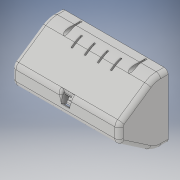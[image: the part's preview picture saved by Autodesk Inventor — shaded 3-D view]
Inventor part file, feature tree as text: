
AUTODESK INVENTOR PART (.ipt)
format: ipt  version: 2018 (Build 220112000, 112)  size: 763,904 bytes
history: native  units: in
note: dims shown in document units (in); Inventor stores cm internally (conversion verified against a paired STEP export)
features: extrude x20, sketch x19, fillet x11, chamfer x5, plane x3, draft x2, shell x1
ambient origin geometry x8: Origin, YZ Plane, XZ Plane, XY Plane, X Axis, Y Axis, Z Axis, Center Point
bodies: Solid1 (feature_tree)
feature tree (61):
  extrude  "Extrusion1"  Depth=3.5in
  shell  "Shell1"  Thickness=0.5in
  extrude  "Extrusion2"  Depth=7.6772in TaperAngle=0.0deg
  fillet  "Fillet4"  Radius=0.25in
  fillet  "Fillet5"  Radius=0.25in
  fillet  "Fillet6"  Radius=0.25in
  plane  "Work Plane1"
  extrude  "Extrusion3"  Depth=7.6772in TaperAngle=0.0deg
  extrude  "Extrusion4"  Depth=1.0in
  extrude  "Extrusion5"  Depth=0.315in
  extrude  "Extrusion6"  TaperAngle=90.0deg  [1 undecoded]
  plane  "Work Plane2"
  fillet  "Fillet13"  Radius=0.5157in
  fillet  "Fillet14"  Radius=0.6496in
  extrude  "Extrusion8"  Depth=1.0in TaperAngle=0.0deg
  extrude  "Extrusion9"  Depth=0.6496in
  extrude  "Extrusion10"  Depth=0.5in
  extrude  "Extrusion11"  Depth=0.5in
  extrude  "Extrusion12"  Depth=0.5709in TaperAngle=0.0deg
  chamfer  "Chamfer4"  Distance=0.2756in
  extrude  "Extrusion13"  Depth=0.1969in
  plane  "Work Plane3"
  extrude  "Extrusion15"  Depth=6.5in
  extrude  "Extrusion16"  Depth=0.125in TaperAngle=0.0deg
  fillet  "Fillet15"  Radius=0.25in
  chamfer  "Chamfer5"  Distance=0.125in
  extrude  "Extrusion17"  Depth=0.1181in
  fillet  "Fillet16"  Radius=0.1181in
  extrude  "Extrusion22"  Depth=0.5in TaperAngle=0.0deg
  extrude  "Extrusion23"  Depth=0.1181in
  fillet  "Fillet22"  Radius=0.7874in
  fillet  "Fillet23"  Radius=0.5in
  chamfer  "Chamfer7"  Distance=0.7874in
  fillet  "Fillet24"  Radius=1.0in
  fillet  "Fillet25"  Radius=0.1181in
  chamfer  "Chamfer9"  Distance=0.7874in
  chamfer  "Chamfer10"  Distance=1.0in
  extrude  "Extrusion27"  Depth=0.1181in
  extrude  "Extrusion28"  Depth=0.7874in
  draft  "FaceDraft1"
  draft  "FaceDraft2"
  extrude  "Extrusion14"  Depth=0.0394in
  sketch  "Sketch1"  dims[d0=4.4094in d1=3.5in d2=0.5in]
  sketch  "Sketch2"  dims[d3=0.5in d4=7.6772in d5=0.0in d6=0.25in d7=0.25in d8=0.25in]
  sketch  "Sketch4"  dims[d10=0.25in d11=7.6772in d12=0.0in]
  sketch  "Sketch5"  dims[d13=1.0in d14=1.0in]
  sketch  "Sketch6"  dims[d18=0.4724in d19=0.315in]
  sketch  "Sketch8"  dims[d20=1.5748in d21=90.0deg d22=0.5157in d23=0.6496in]
  sketch  "Sketch9"  dims[d24=0.1969in d25=1.0in d26=0.0in]
  sketch  "Sketch10"  dims[d27=0.5157in d28=0.6496in]
  sketch  "Sketch11"  dims[d29=0.2362in d30=0.5in]
  sketch  "Sketch12"  dims[d31=0.125in d32=0.5in]
  sketch  "Sketch13"  dims[d33=0.5709in d34=0.0in d35=0.5709in d36=0.0in d37=0.2756in d38=0.0in]
  sketch  "Sketch14"  dims[d44=0.8in d60=0.1969in]
  sketch  "Sketch15"  dims[d61=0.1181in d62=6.5in]
  sketch  "Sketch16"  dims[d63=2.5in d64=0.125in d65=0.0in d66=0.25in]
  sketch  "Sketch17"  dims[d67=0.25in d68=0.125in d69=0.0in]
  sketch  "Sketch23"  dims[d70=0.1181in d71=0.1181in d72=0.1181in]
  sketch  "Sketch25"  dims[d73=0.1181in d74=0.5in d75=0.0in]
  sketch  "Sketch29"  dims[d76=0.5in d77=0.1181in d78=0.7874in d79=0.5in]
  sketch  "Sketch30"  dims[d80=0.1181in d81=0.7874in d82=1.0in d83=0.1181in d84=0.7874in d85=1.0in d86=0.1181in d87=0.7874in d88=0.0394in d89=1.0in d90=0.0in d91=0.25in d92=0.0in d93=2.3622in d94=1.0in d95=0.1575in d96=0.0in d97=0.1575in d98=0.125in d99=45.0deg d100=1.2894in d101=4.9606in d102=0.1181in d103=0.1181in d104=0.1181in d105=0.1181in d106=2.0in d107=0.0in d108=-1.5in d109=0.2756in d110=0.2756in d111=0.2756in d112=0.2756in d113=1.378in d114=0.0in d115=0.0in d116=2.3622in d117=1.5748in d118=0.1575in d119=0.0in d120=0.6102in d121=0.2657in d122=0.0787in d123=0.0787in d124=0.0787in d125=0.0787in d126=0.1969in d127=0.1969in d128=0.1969in d129=0.1969in d130=0.1181in d131=0.0in d132=0.0787in d133=0.1575in d134=0.125in d135=45.0deg d136=0.0787in d138=1.136in d139=0.2568in d140=0.2568in d141=0.2362in d142=0.0in d149=0.1181in d150=0.1181in d153=0.2362in d154=0.0in d159=0.0in d161=0.0in d162=3.0in d163=0.0in d164=0.2362in d168=0.2028in d170=0.0787in d171=0.0197in d172=0.315in d173=0.125in d174=45.0deg d178=0.0in d179=0.1969in d180=0.1969in d181=0.0in d182=0.0787in d183=0.125in d184=45.0deg d185=0.0787in d186=0.125in d187=45.0deg d197=0.8661in d198=0.1181in d199=0.0in d200=0.8661in d201=0.1181in d202=0.0in d203=-0.0344in d204=-0.0344in d205=0.9646in d206=1.3583in d207=0.4823in d208=0.4823in d209=0.6791in d210=0.6791in d211=0.125in]
note: 1 required parameter value undecoded (feature->parameter linkage not recoverable at this tier; creation-order binding heuristic only, values carry confidence <= 0.55)
